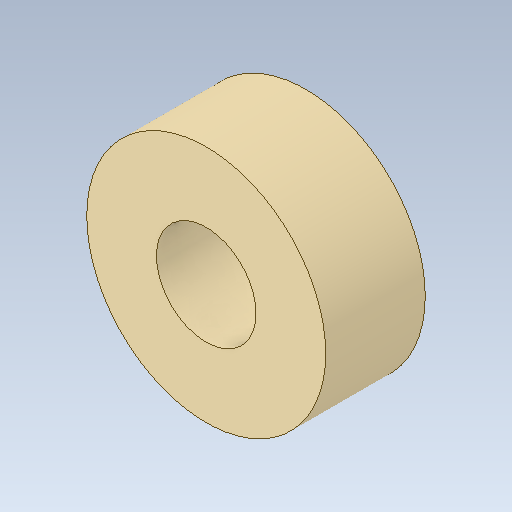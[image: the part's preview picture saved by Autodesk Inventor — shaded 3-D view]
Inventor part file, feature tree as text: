
AUTODESK INVENTOR PART (.ipt)
format: ipt  version: 2020 (Build 240168000, 168)  size: 97,792 bytes
history: native  units: mm
features: other x1, extrude x1, sketch x1
ambient origin geometry x8: Origin, YZ Plane, XZ Plane, XY Plane, X Axis, Y Axis, Z Axis, Center Point
bodies: Body1 (feature_tree)
feature tree (3):
  other  "Твердое тело1"
  extrude  "Выдавливание1"  Depth=5.0mm TaperAngle=0.0deg
  sketch  "Эскиз1"
